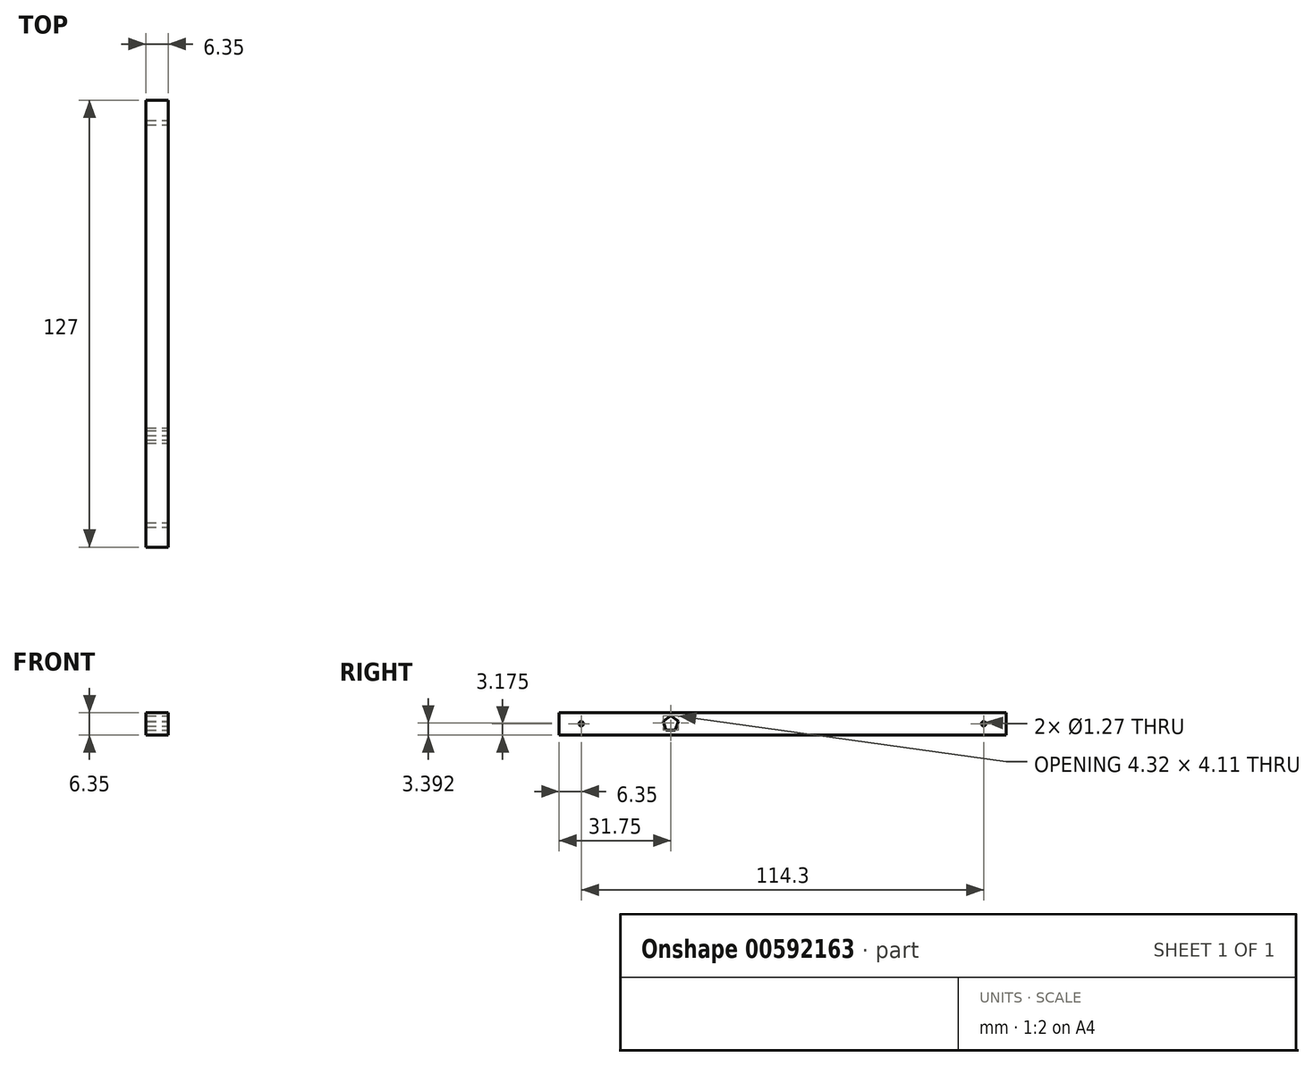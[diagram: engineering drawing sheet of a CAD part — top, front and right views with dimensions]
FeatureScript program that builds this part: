
annotation { "Feature Type Name" : "Feature", "Feature Type Description" : "" }
export const myFeature = defineFeature(function(context is Context, id is Id, definition is map)
    precondition{}
    {
        {
            var Q0;
            Q0=qCreatedBy(makeId("Top.planeOp"),FACE);
            var sketch = newSketch(context, id + "F0", { "sketchPlane" : qUnion([Q0])});
            skLineSegment(sketch, "E0.bottom", {"start": v(0, 0) * mm, "end": v(6.35, 0) * mm});
            skLineSegment(sketch, "E0.top", {"start": v(0, 127) * mm, "end": v(6.35, 127) * mm});
            skLineSegment(sketch, "E0.left", {"start": v(0, 0) * mm, "end": v(0, 127) * mm});
            skLineSegment(sketch, "E0.right", {"start": v(6.35, 0) * mm, "end": v(6.35, 127) * mm});
            skSolve(sketch);
        }
        {
            var Q0;
            Q0 = qSketchRegion(id + "F0", true);
            extrude(context, id + "F1", {"entities" : qUnion([Q0]), "depth" : 6.35 * mm, "offsetDistance" : 25.4 * mm});
        }
        {
            var Q0;
            Q0=makeQuery(id+"F1.opExtrude","SWEPT_FACE",FACE,{"disambiguationData":[OSD([sQuery(id+"F0.wireOp",EDGE,"E0.right")])]});
            var sketch = newSketch(context, id + "F2", { "sketchPlane" : qUnion([Q0])});
            skCircle(sketch, "E1.cCircle", {"center": v(31.75, 3.17) * mm, "radius": 2.27 * mm, "construction": true});
            skLineSegment(sketch, "E1.0", {"start": v(33.91, 3.88) * mm, "end": v(33.09, 1.34) * mm});
            skLineSegment(sketch, "E1.1", {"start": v(33.09, 1.34) * mm, "end": v(30.41, 1.34) * mm});
            skLineSegment(sketch, "E1.2", {"start": v(30.41, 1.34) * mm, "end": v(29.59, 3.88) * mm});
            skLineSegment(sketch, "E1.3", {"start": v(29.59, 3.88) * mm, "end": v(31.75, 5.45) * mm});
            skLineSegment(sketch, "E1.4", {"start": v(31.75, 5.45) * mm, "end": v(33.91, 3.88) * mm});
            skLineSegment(sketch, "E2", {"start": v(31.75, 3.18) * mm, "end": v(31.75, 6.35) * mm});
            skLineSegment(sketch, "E3", {"start": v(31.75, 6.35) * mm, "end": v(63.5, 6.35) * mm});
            skLineSegment(sketch, "E4", {"start": v(0, 3.18) * mm, "end": v(6.35, 3.18) * mm});
            skPoint(sketch, "E4.endSnap0", {"position": v(0, 3.18) * mm});
            skCircle(sketch, "E5", {"center": v(6.35, 3.18) * mm, "radius": 0.64 * mm});
            skLineSegment(sketch, "E6", {"start": v(127, 3.18) * mm, "end": v(120.65, 3.18) * mm});
            skCircle(sketch, "E7", {"center": v(120.65, 3.18) * mm, "radius": 0.64 * mm});
            skSolve(sketch);
        }
        {
            var Q0;
            Q0=makeQuery(id+"F2.imprint","IMPRINT",FACE,{"disambiguationData":[TD([[makeQuery(id+"F2.imprint","IMPRINT",EDGE,{"derivedFrom":sQuery(id+"F2.wireOp",EDGE,"E5")}),1.0]])]});
            var Q1;
            Q1=makeQuery(id+"F2.imprint","IMPRINT",FACE,{"disambiguationData":[TD([[makeQuery(id+"F2.imprint","IMPRINT",EDGE,{"derivedFrom":sQuery(id+"F2.wireOp",EDGE,"E1.0")}),-1.0]])]});
            var Q2;
            Q2=makeQuery(id+"F2.imprint","IMPRINT",FACE,{"disambiguationData":[TD([[makeQuery(id+"F2.imprint","IMPRINT",EDGE,{"derivedFrom":sQuery(id+"F2.wireOp",EDGE,"E7")}),1.0]])]});
            extrude(context, id + "F3", {"entities" : qUnion([Q0, Q1, Q2]), "operationType" : NewBodyOperationType.REMOVE, "endBound" : BoundingType.THROUGH_ALL, "oppositeDirection" : true, "depth" : 25.4 * mm, "offsetDistance" : 25.4 * mm});
        }
    });
